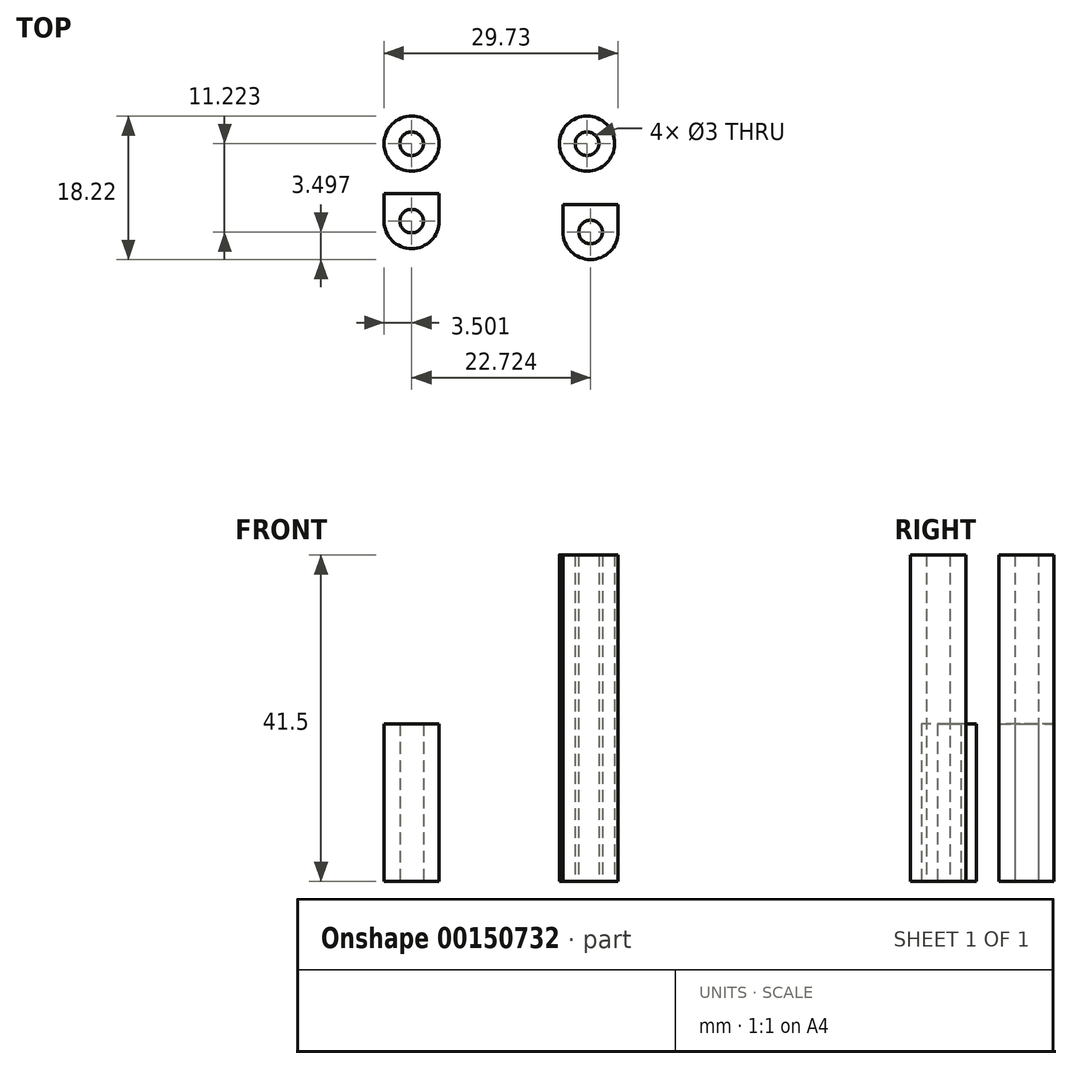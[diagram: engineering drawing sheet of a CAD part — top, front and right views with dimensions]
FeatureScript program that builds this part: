
annotation { "Feature Type Name" : "Feature", "Feature Type Description" : "" }
export const myFeature = defineFeature(function(context is Context, id is Id, definition is map)
    precondition{}
    {
        {
            var Q0;
            Q0=qCreatedBy(makeId("Top.planeOp"),FACE);
            var sketch = newSketch(context, id + "F0", { "sketchPlane" : qUnion([Q0])});
            skCircle(sketch, "E0", {"center": v(-13.29, 0) * mm, "radius": 3.5 * mm});
            skCircle(sketch, "E1", {"center": v(-13.29, 0) * mm, "radius": 1.5 * mm});
            skCircle(sketch, "E2", {"center": v(-13.29, -9.84) * mm, "radius": 1.5 * mm});
            skLineSegment(sketch, "E3", {"start": v(-16.79, -6.34) * mm, "end": v(-16.79, -9.84) * mm});
            skLineSegment(sketch, "E4", {"start": v(-9.79, -6.34) * mm, "end": v(-9.79, -9.84) * mm});
            skArc(sketch, "E5", {"start": v(-9.79, -9.84) * mm, "mid": v(-13.29, -13.34) * mm, "end": v(-16.79, -9.84) * mm});
            skLineSegment(sketch, "E6", {"start": v(-16.79, -6.34) * mm, "end": v(-9.79, -6.34) * mm});
            skSolve(sketch);
        }
        {
            var Q0;
            Q0=makeQuery(id+"F0.imprint","IMPRINT",FACE,{"disambiguationData":[TD([[makeQuery(id+"F0.imprint","IMPRINT",EDGE,{"derivedFrom":sQuery(id+"F0.wireOp",EDGE,"E0")}),1.0]])]});
            var Q1;
            Q1=makeQuery(id+"F0.imprint","IMPRINT",FACE,{"disambiguationData":[TD([[makeQuery(id+"F0.imprint","IMPRINT",EDGE,{"derivedFrom":sQuery(id+"F0.wireOp",EDGE,"E2")}),-1.0]])]});
            extrude(context, id + "F1", {"entities" : qUnion([Q0, Q1]), "depth" : 20 * mm});
        }
        {
            var Q0;
            Q0=qCreatedBy(makeId("Top.planeOp"),FACE);
            var sketch = newSketch(context, id + "F2", { "sketchPlane" : qUnion([Q0])});
            skCircle(sketch, "E7", {"center": v(8.99, 0) * mm, "radius": 3.5 * mm});
            skCircle(sketch, "E8", {"center": v(8.99, 0) * mm, "radius": 1.5 * mm});
            skLineSegment(sketch, "E9", {"start": v(5.94, -7.72) * mm, "end": v(12.94, -7.72) * mm});
            skLineSegment(sketch, "E10", {"start": v(12.94, -7.72) * mm, "end": v(12.94, -11.22) * mm});
            skLineSegment(sketch, "E11", {"start": v(5.94, -7.72) * mm, "end": v(5.94, -11.22) * mm});
            skArc(sketch, "E12", {"start": v(12.94, -11.22) * mm, "mid": v(9.44, -14.72) * mm, "end": v(5.94, -11.22) * mm});
            skPoint(sketch, "E12.centerSnap0", {"position": v(9.44, -7.72) * mm});
            skCircle(sketch, "E13", {"center": v(9.44, -11.22) * mm, "radius": 1.5 * mm});
            skSolve(sketch);
        }
        {
            var Q0;
            Q0=makeQuery(id+"F2.imprint","IMPRINT",FACE,{"disambiguationData":[TD([[makeQuery(id+"F2.imprint","IMPRINT",EDGE,{"derivedFrom":sQuery(id+"F2.wireOp",EDGE,"E7")}),1.0]])]});
            var Q1;
            Q1=makeQuery(id+"F2.imprint","IMPRINT",FACE,{"disambiguationData":[TD([[makeQuery(id+"F2.imprint","IMPRINT",EDGE,{"derivedFrom":sQuery(id+"F2.wireOp",EDGE,"E9")}),-1.0]])]});
            extrude(context, id + "F3", {"entities" : qUnion([Q0, Q1]), "depth" : 41.5 * mm});
        }
    });
